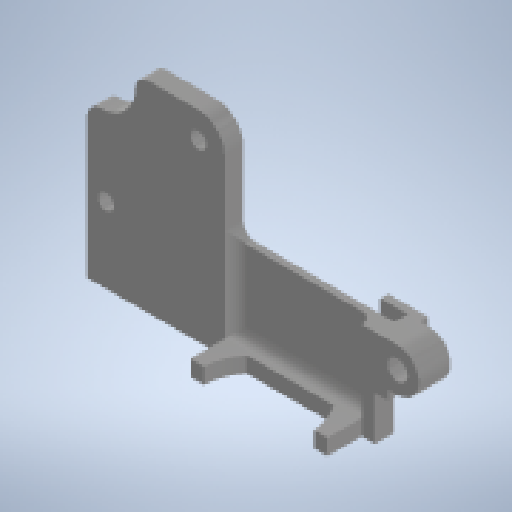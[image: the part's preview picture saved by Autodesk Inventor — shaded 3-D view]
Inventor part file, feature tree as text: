
AUTODESK INVENTOR PART (.ipt)
format: ipt  version: 2023 (Build 270158000, 158)  size: 294,400 bytes
history: native  units: in
note: dims shown in document units (in); Inventor stores cm internally (conversion verified against a paired STEP export)
features: extrude x8, reference x7, sketch x7, other x5, fillet x1, projected_geometry x1
ambient origin geometry x8: Origin, YZ Plane, XZ Plane, XY Plane, X Axis, Y Axis, Z Axis, Center Point
bodies: Solid1 (feature_tree)
feature tree (29):
  extrude  "Extrusion1"  TaperAngle=90.0deg  [1 undecoded]
  extrude  "Extrusion2"  Depth=0.1378in
  fillet  "Fillet1"  [1 undecoded]
  extrude  "Extrusion3"  Depth=0.185in
  extrude  "Extrusion4"  Depth=0.1181in
  extrude  "Extrusion5"  Depth=0.1181in
  extrude  "Extrusion7"  Depth=0.0866in
  extrude  "Extrusion9"  Depth=0.0591in
  extrude  "Extrusion10"  Depth=0.1181in TaperAngle=0.0deg
  reference  "Reference1"
  reference  "Reference2"
  reference  "Reference4"
  reference  "Reference5"
  sketch  "Sketch2"  dims[d0=90.0deg d1=90.0deg]
  sketch  "Sketch3"  dims[d2=0.0787in d3=0.1378in d5=90.0deg]
  reference  "Reference6"
  sketch  "Sketch4"  dims[d6=90.0deg d7=0.185in]
  reference  "Reference7"
  sketch  "Sketch5"  dims[d12=0.1378in d13=0.0in d14=0.1181in]
  sketch  "Sketch8"  dims[d15=0.1181in d16=0.9843in]
  sketch  "Sketch9"  dims[d18=0.0866in d19=0.0in d21=0.0787in]
  sketch  "Sketch10"  dims[d22=0.0157in d23=0.0157in d24=0.1181in d25=0.0in d27=0.1594in d28=0.0in d30=0.1969in d31=0.0in d35=0.1339in d36=0.0945in d37=0.0689in d38=0.2362in d39=0.0in d42=0.2244in d43=0.2362in d44=0.1181in d45=0.0in d46=0.0in d47=0.0059in d48=0.3937in d49=0.0in d51=0.0984in d52=0.3937in d53=0.0984in d54=0.1181in d55=0.2559in d57=0.0591in d56=0.0344in]
  reference  "Reference10"
  projected_geometry  "Projected Loop1"
  other  "<userpath>\Desktop\Another3dPrinterShroud\MODELS\ENDER 3 ASSEMBLY ALTDUCT.iam"
  other  "ENDER 3 ASSEMBLY ALTDUCT.iam"
  other  "ENDER 3 E_PLATE_SCREW:1"
  other  "ENDER 3 E_PLATE:1"
  other  "ENDER 3 RAD:1"
note: 2 required parameter values undecoded (feature->parameter linkage not recoverable at this tier; creation-order binding heuristic only, values carry confidence <= 0.55)
